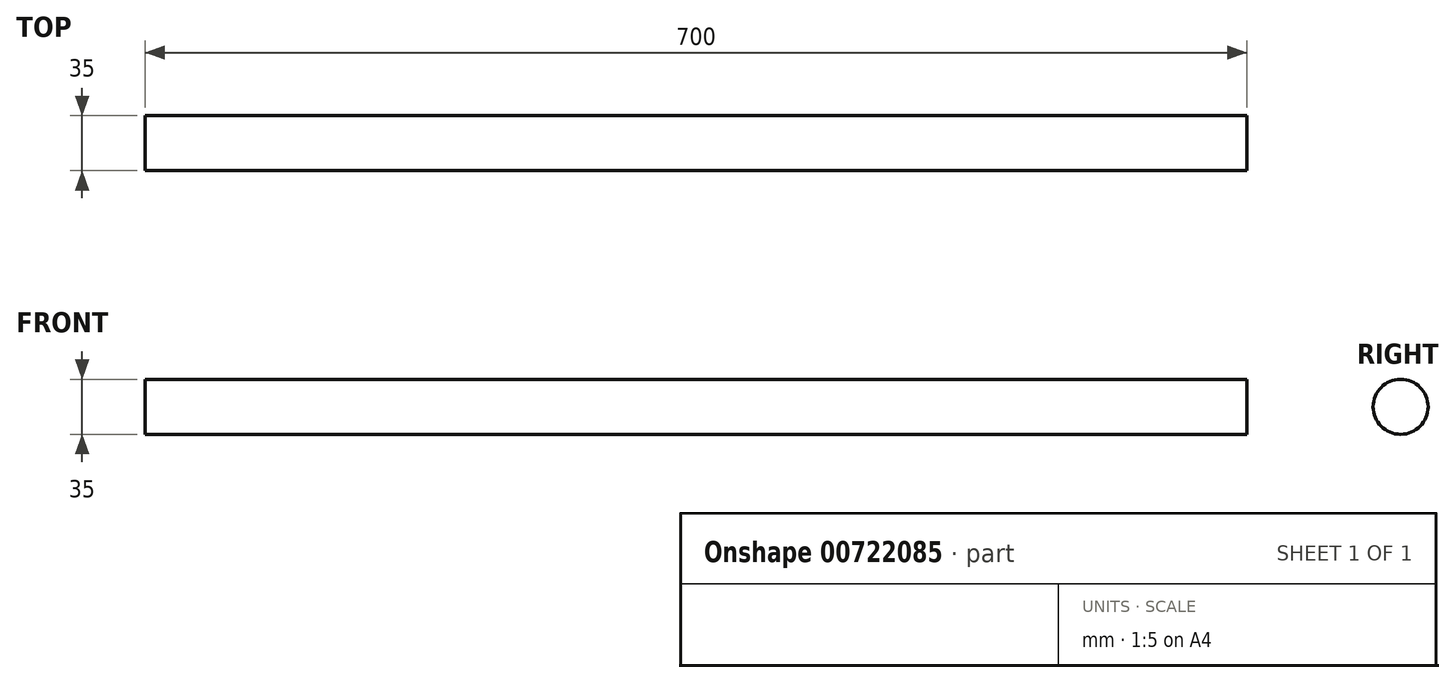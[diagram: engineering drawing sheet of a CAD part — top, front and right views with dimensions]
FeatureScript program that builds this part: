
annotation { "Feature Type Name" : "Feature", "Feature Type Description" : "" }
export const myFeature = defineFeature(function(context is Context, id is Id, definition is map)
    precondition{}
    {
        {
            var Q0;
            Q0=qCreatedBy(makeId("Right.planeOp"),FACE);
            var sketch = newSketch(context, id + "F0", { "sketchPlane" : qUnion([Q0])});
            skCircle(sketch, "E0", {"center": v(0, 0) * mm, "radius": 17.5 * mm});
            skCircle(sketch, "E1", {"center": v(0, 0) * mm, "radius": 15.5 * mm});
            skSolve(sketch);
        }
        {
            var Q0;
            Q0=makeQuery(id+"F0.imprint","IMPRINT",FACE,{"disambiguationData":[TD([[makeQuery(id+"F0.imprint","IMPRINT",EDGE,{"derivedFrom":sQuery(id+"F0.wireOp",EDGE,"E0")}),1.0]])]});
            var Q1;
            Q1=makeQuery(id+"F0.imprint","IMPRINT",FACE,{"disambiguationData":[TD([[makeQuery(id+"F0.imprint","IMPRINT",EDGE,{"derivedFrom":sQuery(id+"F0.wireOp",EDGE,"E1")}),1.0]])]});
            extrude(context, id + "F1", {"entities" : qUnion([Q0, Q1]), "depth" : 700 * mm, "offsetDistance" : 25 * mm});
        }
    });
